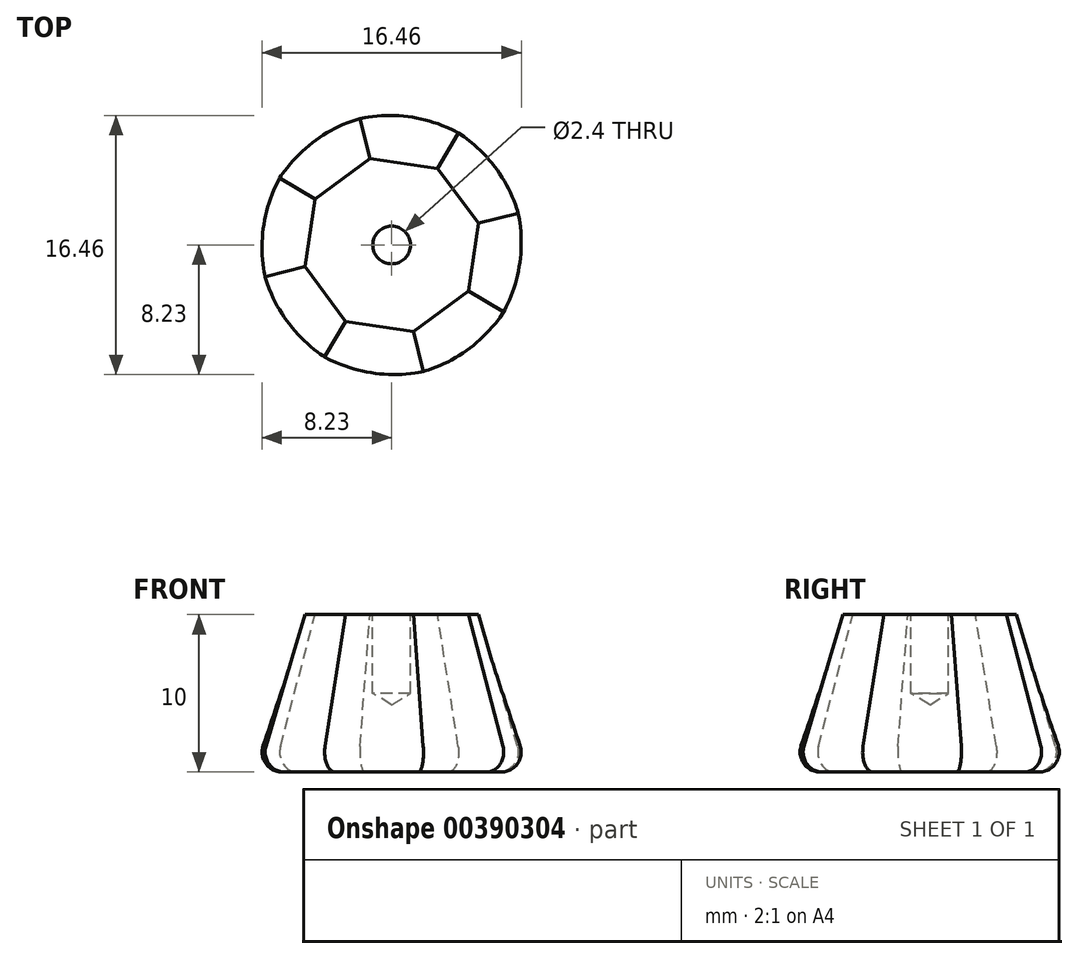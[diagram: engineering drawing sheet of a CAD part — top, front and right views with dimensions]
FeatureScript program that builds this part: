
annotation { "Feature Type Name" : "Feature", "Feature Type Description" : "" }
export const myFeature = defineFeature(function(context is Context, id is Id, definition is map)
    precondition{}
    {
        {
            var Q0;
            Q0=qCreatedBy(makeId("Top.planeOp"),FACE);
            var sketch = newSketch(context, id + "F0", { "sketchPlane" : qUnion([Q0])});
            skCircle(sketch, "E0", {"center": v(0, 0) * mm, "radius": 8.74 * mm});
            skSolve(sketch);
        }
        {
            var Q0;
            Q0=makeQuery(id+"F0.imprint","IMPRINT",FACE,{"disambiguationData":[TD([[makeQuery(id+"F0.imprint","IMPRINT",EDGE,{"derivedFrom":sQuery(id+"F0.wireOp",EDGE,"E0")}),1.0]])]});
            cPlane(context, id + "F1", {"entities" : qUnion([Q0]), "cplaneType" : CPlaneType.OFFSET, "offset" : 10 * mm, "width" : 152.4 * mm, "height" : 152.4 * mm});
        }
        {
            var Q0;
            Q0=qCreatedBy(id+"F1.planeOp",FACE);
            var sketch = newSketch(context, id + "F2", { "sketchPlane" : qUnion([Q0])});
            skCircle(sketch, "E1.cCircle", {"center": v(0, 0) * mm, "radius": 5.24 * mm, "construction": true});
            skLineSegment(sketch, "E1.0", {"start": v(4.87, -2.91) * mm, "end": v(1.38, -5.5) * mm});
            skLineSegment(sketch, "E1.1", {"start": v(1.38, -5.5) * mm, "end": v(-2.91, -4.87) * mm});
            skLineSegment(sketch, "E1.2", {"start": v(-2.91, -4.87) * mm, "end": v(-5.5, -1.38) * mm});
            skLineSegment(sketch, "E1.3", {"start": v(-5.5, -1.38) * mm, "end": v(-4.87, 2.91) * mm});
            skLineSegment(sketch, "E1.4", {"start": v(-4.87, 2.91) * mm, "end": v(-1.38, 5.5) * mm});
            skLineSegment(sketch, "E1.5", {"start": v(-1.38, 5.5) * mm, "end": v(2.91, 4.87) * mm});
            skLineSegment(sketch, "E1.6", {"start": v(2.91, 4.87) * mm, "end": v(5.5, 1.38) * mm});
            skLineSegment(sketch, "E1.7", {"start": v(5.5, 1.38) * mm, "end": v(4.87, -2.91) * mm});
            skPoint(sketch, "E1.0.midPoint", {"position": v(3.13, -4.2) * mm});
            skSolve(sketch);
        }
        {
            var Q0;
            Q0=makeQuery(id+"F0.imprint","IMPRINT",FACE,{"disambiguationData":[TD([[makeQuery(id+"F0.imprint","IMPRINT",EDGE,{"derivedFrom":sQuery(id+"F0.wireOp",EDGE,"E0")}),1.0]])]});
            var Q1;
            Q1=makeQuery(id+"F2.imprint","IMPRINT",FACE,{"disambiguationData":[TD([[makeQuery(id+"F2.imprint","IMPRINT",EDGE,{"derivedFrom":sQuery(id+"F2.wireOp",EDGE,"E1.0")}),-1.0]])]});
            loft(context, id + "F3", {"sheetProfilesArray" : [{ "sheetProfileEntities" : qUnion([Q0]) }, { "sheetProfileEntities" : qUnion([Q1]) }]});
        }
        {
            var Q0;
            Q0=sQuery(id+"F2.wireOp",VERTEX,"E1.cCircle.center");
            var Q1;
            Q1=makeQuery(id+"F3.opLoft","SWEPT_BODY",BODY,{"disambiguationData":[OSD([makeQuery(id+"F0.imprint","IMPRINT",FACE,{"disambiguationData":[TD([[makeQuery(id+"F0.imprint","IMPRINT",EDGE,{"derivedFrom":sQuery(id+"F0.wireOp",EDGE,"E0")}),1.0]])]}),makeQuery(id+"F2.imprint","IMPRINT",FACE,{"disambiguationData":[TD([[makeQuery(id+"F2.imprint","IMPRINT",EDGE,{"derivedFrom":sQuery(id+"F2.wireOp",EDGE,"E1.0")}),-1.0]])]})])]});
            hole(context, id + "F4", {"style" : HoleStyle.SIMPLE, "endStyle" : HoleEndStyle.BLIND, "holeDiameter" : 2.4 * mm, "holeDepth" : 5 * mm, "isTappedThrough" : true, "tappedDepth" : 12.7 * mm, "tapClearance" : 3, "locations" : qUnion([Q0]), "scope" : qUnion([Q1])});
        }
        {
            var Q0;
            Q0=makeQuery(id+"F3.opLoft","CAP_FACE",FACE,{"disambiguationData":[OSD([makeQuery(id+"F0.imprint","IMPRINT",FACE,{"disambiguationData":[TD([[makeQuery(id+"F0.imprint","IMPRINT",EDGE,{"derivedFrom":sQuery(id+"F0.wireOp",EDGE,"E0")}),1.0]])]})])],"isStart":true});
            fillet(context, id + "F5", {"entities" : qUnion([Q0]), "radius" : 1.27 * mm, "tangentPropagation" : true, "allowEdgeOverflow" : false});
        }
    });
